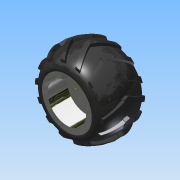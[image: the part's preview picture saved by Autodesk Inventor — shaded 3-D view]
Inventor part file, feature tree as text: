
AUTODESK INVENTOR PART (.ipt)
format: ipt  version: 2014 (Build 180170000, 170)  size: 1,011,712 bytes
history: native  units: in
note: dims shown in document units (in); Inventor stores cm internally (conversion verified against a paired STEP export)
features: sketch x10, extrude x8, projected_geometry x4, revolve x2, plane x2, mirror x2, pattern_circular x1
ambient origin geometry x8: Origin, YZ Plane, XZ Plane, XY Plane, X Axis, Y Axis, Z Axis, Center Point
bodies: Solid1 (feature_tree)
feature tree (29):
  extrude  "Extrusion1"  Depth=2.84in
  extrude  "Extrusion2"  Depth=0.326in TaperAngle=0.0deg
  extrude  "Extrusion3"  Depth=0.15in
  extrude  "Extrusion4"  Depth=2.6in
  extrude  "Extrusion5"  Depth=0.3in
  extrude  "Extrusion6"  Depth=1.33in
  revolve  "Revolution1"  [1 undecoded]
  extrude  "Extrusion7"  Depth=1.1811in TaperAngle=360.0deg
  plane  "Work Plane1"
  extrude  "Extrusion8"  Depth=0.26in
  plane  "Work Plane2"
  pattern_circular  "Circular Pattern1"  [2 undecoded]
  mirror  "Mirror1"
  revolve  "Revolution2"  Angle=90.0deg
  mirror  "Mirror2"
  sketch  "Sketch1"  dims[d0=2.6in d1=2.84in]
  sketch  "Sketch2"  dims[d2=1.48in d3=0.0in d4=0.326in d5=0.0in]
  sketch  "Sketch3"  dims[d6=0.824in d7=0.15in]
  sketch  "Sketch4"  dims[d8=0.31in d9=0.0in d10=2.6in]
  sketch  "Sketch5"  dims[d11=1.314in d12=0.0in d13=0.3in]
  sketch  "Sketch6"  dims[d14=0.41in d15=0.0in d16=1.33in]
  sketch  "Sketch7"  dims[d17=0.05in d18=0.05in]
  sketch  "Sketch8"  dims[d19=0.025in d20=1.1811in d22=360.0deg]
  sketch  "Sketch9"  dims[d24=0.32in d25=0.0in d26=0.26in]
  sketch  "Sketch10"  dims[d27=0.26in d31=5.0in d32=90.0deg d33=0.375in d34=0.6575in d35=3.1496in d37=360.0deg d39=0.21in d40=0.0in d41=2.7in d42=0.32in d44=0.72in d45=1.65in d46=0.2in d47=0.3in d48=0.165in d49=1.0in d50=0.0in d51=5.5118in d52=360.0deg d54=-1.56in d55=90.0deg d56=2.7863in]
  projected_geometry  "Project Cut Edges1"
  projected_geometry  "Project Cut Edges2"
  projected_geometry  "Project Cut Edges3"
  projected_geometry  "Project Cut Edges4"
note: 3 required parameter values undecoded (feature->parameter linkage not recoverable at this tier; creation-order binding heuristic only, values carry confidence <= 0.55)